# Revit family: 147016821_Mueble Vital Vessel 60 cm Elevado con Lavamanos
name_source: partatom
category: Furniture
units: mm (PartAtom-declared; Revit-internal decimal feet)

## family parameters
Always vertical = Yes
Cut with Voids When Loaded = No
OmniClass Number = 23.31.13.11
OmniClass Title = Single Sinks
Room Calculation Point = No
Shared = No
Work Plane-Based = No

## types (1)
- 147016821_Mueble Vital Vessel 60 cm Elevado con Lavamanos
    Acabado = Corona_Madera_Blanco
    Alto = 864 mm  [stored 2.83465 ft]
    Ancho = 600 mm  [stored 1.9685 ft]
    Creado por = IDD
    Description = Mueble Plus Vessel con acabado de pintura blanca brillante que da mayor
amplitud a espacios reducidos.
· Repisas visibles para almacenamiento de fácil acceso.
· Máxima capacidad de almacenamiento.
· Lavamanos 100% en porcelana.
· Resistentes a la humedad.
    Fecha de creación = 30/07/2020
    Garantía = 1 Años de garantia (Madera)
    Garantía Herraje = 1 Años
    Longitud = 450 mm  [stored 1.47638 ft]
    Manija = Corona_Aluminio
    Manufacturer = Corona
    Material = Corona_Madera_Aglomerada_Duna
    Model = Plus Vessel 60
    Peso Bruto aprox = 38,1 lb (17,3 kg).
    Peso Neto aprox = 13,4 lb (16,4 kg).
    Resistencia a la humedad = 8%.

note: [stored X ft] marks values corroborated as IEEE doubles in the binary element streams (Revit-internal decimal feet)

## geometry (parser evidence)
native form markers: Sweep x8
no freeform markers — native parametric forms only
